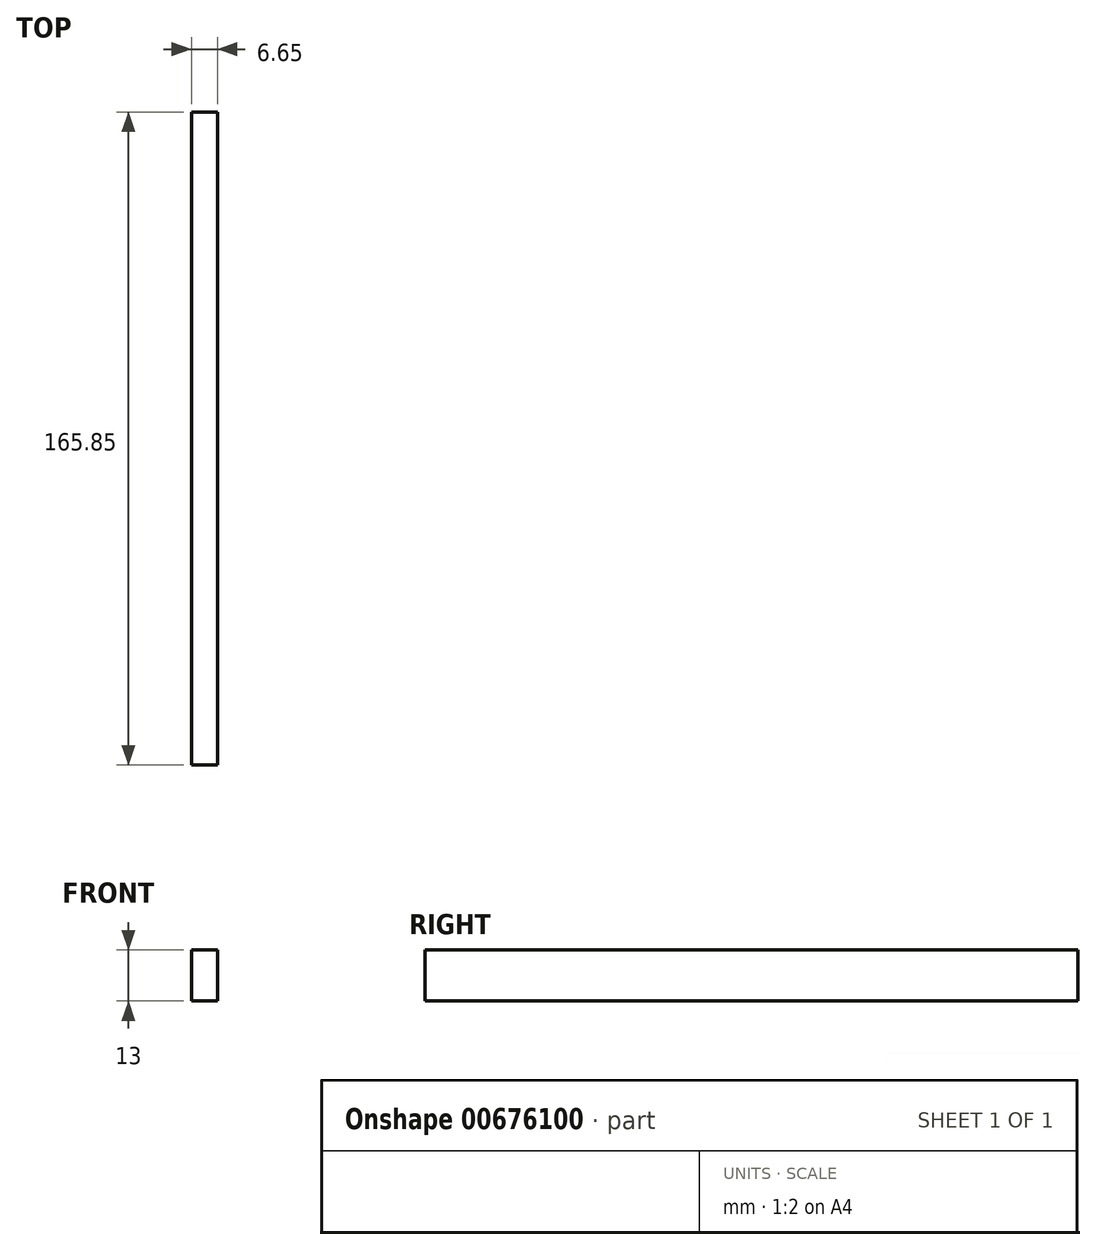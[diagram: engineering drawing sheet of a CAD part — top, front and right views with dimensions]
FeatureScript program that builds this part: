
annotation { "Feature Type Name" : "Feature", "Feature Type Description" : "" }
export const myFeature = defineFeature(function(context is Context, id is Id, definition is map)
    precondition{}
    {
        {
            var Q0;
            Q0=qCreatedBy(makeId("Front.planeOp"),FACE);
            var sketch = newSketch(context, id + "F0", { "sketchPlane" : qUnion([Q0])});
            skLineSegment(sketch, "E0.bottom", {"start": v(0, 0) * mm, "end": v(6.65, 0) * mm});
            skLineSegment(sketch, "E0.top", {"start": v(0, 13) * mm, "end": v(6.65, 13) * mm});
            skLineSegment(sketch, "E0.left", {"start": v(0, 0) * mm, "end": v(0, 13) * mm});
            skLineSegment(sketch, "E0.right", {"start": v(6.65, 0) * mm, "end": v(6.65, 13) * mm});
            skSolve(sketch);
        }
        {
            var Q0;
            Q0 = qSketchRegion(id + "F0", true);
            extrude(context, id + "F1", {"entities" : qUnion([Q0]), "depth" : 165.85 * mm, "offsetDistance" : 25 * mm});
        }
    });
